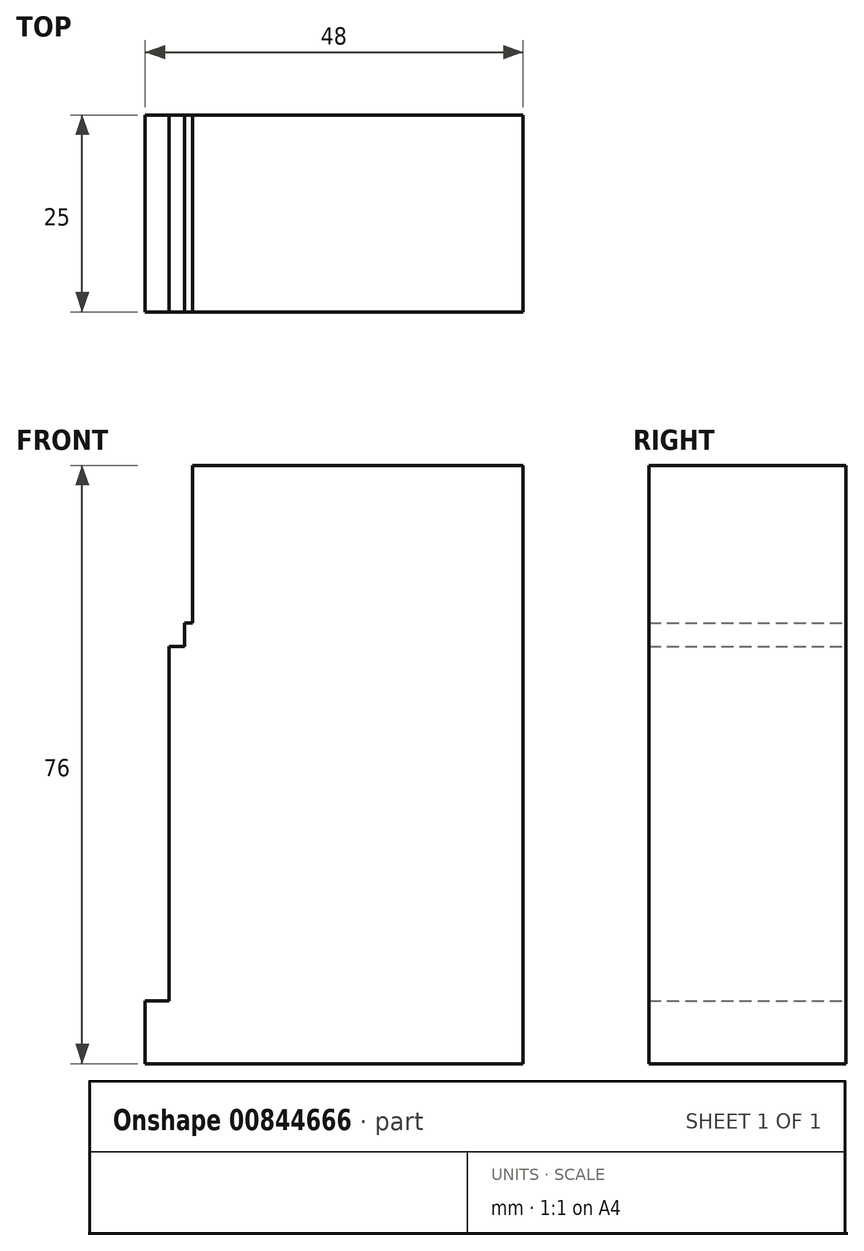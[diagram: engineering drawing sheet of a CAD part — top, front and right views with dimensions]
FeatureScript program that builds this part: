
annotation { "Feature Type Name" : "Feature", "Feature Type Description" : "" }
export const myFeature = defineFeature(function(context is Context, id is Id, definition is map)
    precondition{}
    {
        {
            var Q0;
            Q0=qCreatedBy(makeId("Front.planeOp"),FACE);
            var sketch = newSketch(context, id + "F0", { "sketchPlane" : qUnion([Q0])});
            skLineSegment(sketch, "E0.bottom", {"start": v(0, 0) * mm, "end": v(-43, 0) * mm});
            skLineSegment(sketch, "E0.top", {"start": v(0, 3) * mm, "end": v(-43, 3) * mm});
            skLineSegment(sketch, "E0.left", {"start": v(0, 0) * mm, "end": v(0, 3) * mm});
            skLineSegment(sketch, "E0.right", {"start": v(-43, 0) * mm, "end": v(-43, 3) * mm});
            skLineSegment(sketch, "E1.bottom", {"start": v(0, 0) * mm, "end": v(-45, 0) * mm});
            skLineSegment(sketch, "E1.top", {"start": v(0, -45) * mm, "end": v(-45, -45) * mm});
            skLineSegment(sketch, "E1.left", {"start": v(0, 0) * mm, "end": v(0, -45) * mm});
            skLineSegment(sketch, "E1.right", {"start": v(-45, 0) * mm, "end": v(-45, -45) * mm});
            skLineSegment(sketch, "E2.bottom", {"start": v(0, 3) * mm, "end": v(-42, 3) * mm});
            skLineSegment(sketch, "E2.top", {"start": v(0, 23) * mm, "end": v(-42, 23) * mm});
            skLineSegment(sketch, "E2.left", {"start": v(0, 3) * mm, "end": v(0, 23) * mm});
            skLineSegment(sketch, "E2.right", {"start": v(-42, 3) * mm, "end": v(-42, 23) * mm});
            skLineSegment(sketch, "E3.bottom", {"start": v(0, -45) * mm, "end": v(-48, -45) * mm});
            skLineSegment(sketch, "E3.top", {"start": v(0, -53) * mm, "end": v(-48, -53) * mm});
            skLineSegment(sketch, "E3.left", {"start": v(0, -45) * mm, "end": v(0, -53) * mm});
            skLineSegment(sketch, "E3.right", {"start": v(-48, -45) * mm, "end": v(-48, -53) * mm});
            skSolve(sketch);
        }
        {
            var Q0;
            Q0 = qSketchRegion(id + "F0", true);
            extrude(context, id + "F1", {"entities" : qUnion([Q0]), "depth" : 25 * mm, "offsetDistance" : 25 * mm});
        }
    });
